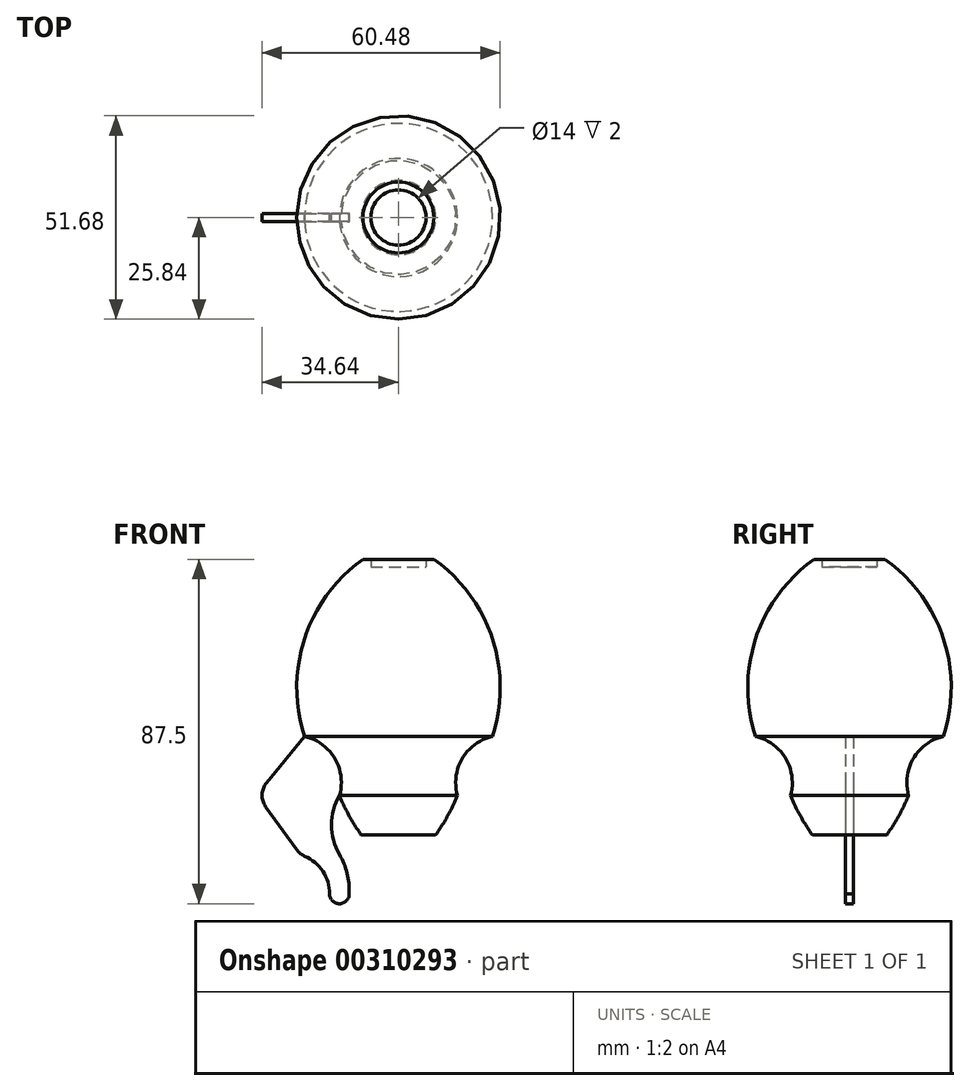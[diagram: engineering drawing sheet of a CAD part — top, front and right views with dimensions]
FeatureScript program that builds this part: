
annotation { "Feature Type Name" : "Feature", "Feature Type Description" : "" }
export const myFeature = defineFeature(function(context is Context, id is Id, definition is map)
    precondition{}
    {
        {
            var Q0;
            Q0=qCreatedBy(makeId("Front.planeOp"),FACE);
            var sketch = newSketch(context, id + "F0", { "sketchPlane" : qUnion([Q0])});
            skLineSegment(sketch, "E0", {"start": v(0, 0) * mm, "end": v(0, 80) * mm});
            skLineSegment(sketch, "E1", {"start": v(0, 80) * mm, "end": v(9, 80) * mm});
            skLineSegment(sketch, "E2", {"start": v(0, 20) * mm, "end": v(15, 20) * mm});
            skLineSegment(sketch, "E3", {"start": v(0, 35) * mm, "end": v(23.88, 35) * mm});
            skArc(sketch, "E4", {"start": v(23.88, 35) * mm, "mid": v(23.82, 59.94) * mm, "end": v(9, 80) * mm});
            skLineSegment(sketch, "E5", {"start": v(0, 78) * mm, "end": v(7, 78) * mm});
            skLineSegment(sketch, "E6", {"start": v(7, 78) * mm, "end": v(7, 80) * mm});
            skArc(sketch, "E7", {"start": v(0, 0) * mm, "mid": v(8.77, 9.05) * mm, "end": v(15, 20) * mm});
            skArc(sketch, "E8", {"start": v(23.88, 35) * mm, "mid": v(16.21, 29.41) * mm, "end": v(15, 20) * mm});
            skSolve(sketch);
        }
        {
            var Q0;
            {var subQ2=sQuery(id+"F0.wireOp",EDGE,"E2");Q0=makeQuery(id+"F0.imprint","IMPRINT",FACE,{"disambiguationData":[TD([[makeQuery(id+"F0.imprint","IMPRINT",EDGE,{"derivedFrom":subQ2}),-1.0]])]});}
            var Q1;
            {var subQ0=sQuery(id+"F0.wireOp",EDGE,"E2");Q1=makeQuery(id+"F0.imprint","IMPRINT",FACE,{"disambiguationData":[TD([[makeQuery(id+"F0.imprint","IMPRINT",EDGE,{"derivedFrom":subQ0}),1.0]])]});}
            var Q2;
            {var subQ3=sQuery(id+"F0.wireOp",EDGE,"E3");Q2=makeQuery(id+"F0.imprint","IMPRINT",FACE,{"disambiguationData":[TD([[makeQuery(id+"F0.imprint","IMPRINT",EDGE,{"derivedFrom":subQ3}),1.0]])]});}
            var Q3;
            Q3=sQuery(id+"F0.wireOp",EDGE,"E0");
            revolve(context, id + "F1", {"entities" : qUnion([Q0, Q1, Q2]), "axis" : qUnion([Q3]), "revolveType" : RevolveType.FULL});
        }
        {
            var Q0;
            Q0=qCreatedBy(makeId("Front.planeOp"),FACE);
            var sketch = newSketch(context, id + "F2", { "sketchPlane" : qUnion([Q0])});
            skLineSegment(sketch, "E9.0", {"start": v(23.88, 35) * mm, "end": v(-23.88, 35) * mm});
            skLineSegment(sketch, "E10.0", {"start": v(15, 20) * mm, "end": v(-15, 20) * mm});
            skArc(sketch, "E11", {"start": v(-15, 20) * mm, "mid": v(-16.21, 29.41) * mm, "end": v(-23.88, 35) * mm});
            skLineSegment(sketch, "E12", {"start": v(-23.88, 35) * mm, "end": v(-15, 20) * mm});
            skLineSegment(sketch, "E13", {"start": v(0, 35) * mm, "end": v(0, 20) * mm});
            skSolve(sketch);
        }
        {
            var Q0;
            Q0 = qSketchRegion(id + "F2", true);
            extrude(context, id + "F3", {"entities" : qUnion([Q0]), "operationType" : NewBodyOperationType.ADD, "endBound" : BoundingType.SYMMETRIC, "depth" : 2 * mm});
        }
        {
            var Q0;
            Q0=qCreatedBy(makeId("Front.planeOp"),FACE);
            var sketch = newSketch(context, id + "F4", { "sketchPlane" : qUnion([Q0])});
            skLineSegment(sketch, "E14", {"start": v(0, 0) * mm, "end": v(0, -5) * mm});
            skLineSegment(sketch, "E15", {"start": v(0, -5) * mm, "end": v(-15, -5) * mm});
            skLineSegment(sketch, "E16", {"start": v(-15, -5) * mm, "end": v(-15, 5) * mm});
            skLineSegment(sketch, "E17", {"start": v(-15, 5) * mm, "end": v(-25, 5) * mm});
            skArc(sketch, "E18", {"start": v(-17.5, -5) * mm, "mid": v(-15, -7.5) * mm, "end": v(-12.5, -5) * mm});
            skLineSegment(sketch, "E19", {"start": v(-15, -5) * mm, "end": v(-17.5, -5) * mm});
            skFitSpline(sketch, "E20.0", {"points": [v(-23.86, 35) * mm, v(-23.46, 34.91) * mm, v(-22.67, 34.69) * mm, v(-21.54, 34.24) * mm, v(-20.46, 33.68) * mm, v(-19.6, 33.13) * mm, v(-18.96, 32.63) * mm, v(-18.34, 32.1) * mm, v(-17.62, 31.39) * mm, v(-16.85, 30.45) * mm, v(-16.16, 29.42) * mm, v(-15.6, 28.35) * mm, v(-15.22, 27.4) * mm, v(-14.97, 26.63) * mm, v(-14.76, 25.84) * mm, v(-14.62, 25.04) * mm, v(-14.53, 24.22) * mm, v(-14.5, 23.4) * mm, v(-14.53, 21.98) * mm, v(-14.74, 20.79) * mm, v(-14.97, 20) * mm]});
            skArc(sketch, "E21", {"start": v(-14.97, 20) * mm, "mid": v(-17, 12.5) * mm, "end": v(-15, 5) * mm});
            skArc(sketch, "E22", {"start": v(-12.5, -5) * mm, "mid": v(-13.05, 0.17) * mm, "end": v(-15, 5) * mm});
            skArc(sketch, "E23", {"start": v(-17.5, -5) * mm, "mid": v(-19.22, 0.73) * mm, "end": v(-23.8, 4.57) * mm});
            skLineSegment(sketch, "E24", {"start": v(-23.86, 35) * mm, "end": v(-33.5, 23.24) * mm});
            skLineSegment(sketch, "E25", {"start": v(-33.7, 17.16) * mm, "end": v(-25.9, 6.25) * mm});
            skPoint(sketch, "E26.visualSharp", {"position": v(-35.94, 20.27) * mm});
            skArc(sketch, "E26.filletArc", {"start": v(-33.5, 23.24) * mm, "mid": v(-34.64, 20.23) * mm, "end": v(-33.7, 17.16) * mm});
            skPoint(sketch, "E27.visualSharp", {"position": v(-25, 5) * mm});
            skArc(sketch, "E27.filletArc", {"start": v(-25.9, 6.25) * mm, "mid": v(-24.97, 5.27) * mm, "end": v(-23.8, 4.57) * mm});
            skSolve(sketch);
        }
        {
            var Q0;
            Q0 = qSketchRegion(id + "F4", true);
            extrude(context, id + "F5", {"entities" : qUnion([Q0]), "operationType" : NewBodyOperationType.ADD, "endBound" : BoundingType.SYMMETRIC, "depth" : 2 * mm});
        }
        {
            var Q0;
            Q0=qCreatedBy(makeId("Top.planeOp"),FACE);
            var sketch = newSketch(context, id + "F6", { "sketchPlane" : qUnion([Q0])});
            skCircle(sketch, "E28", {"center": v(0, 0) * mm, "radius": 10 * mm});
            skSolve(sketch);
        }
        {
            var Q0;
            Q0 = qSketchRegion(id + "F6", true);
            extrude(context, id + "F7", {"entities" : qUnion([Q0]), "operationType" : NewBodyOperationType.REMOVE, "depth" : 10 * mm});
        }
    });
